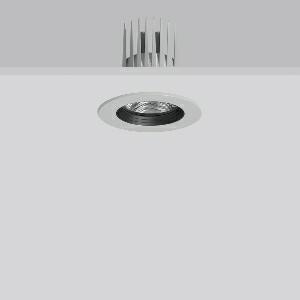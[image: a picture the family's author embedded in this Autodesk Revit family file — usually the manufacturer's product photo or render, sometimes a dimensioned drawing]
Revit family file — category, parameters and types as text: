
# Revit family: heledon_mini_e_901740_004_2_76_123c
name_source: partatom
category: Lighting Fixtures
units: mm (PartAtom-declared; Revit-internal decimal feet)

## family parameters
Cut with Voids When Loaded = No
Host = Face
Light Source = No
Part Type = Normal
Room Calculation Point = No
Round Connector Dimension = Use Diameter
Shared = No

## types (1)
- HELEDON mini E (1 x LED Modul 927, 2400 lm, 2700)
    Apparent Load = 20 VA
    Approval mark = CE
    CIE Flux Codes = 100 100 100 100 100
    Color Rendering = 92
    Color Temperature = 2700
    Default Elevation = 1800 mm
    Description = Series: HELEDON mini
Round recessed downlight. Housing: die-cast aluminium, powder-coated. Black plastic ring and recessed LED to prevent glare from the side. Optical assembly with reflector made of MIRO-Silver with 98% total light reflection for outstanding efficiency - can be changed without tools. Best colour rendering index Ra>90. Suitable for Recessed ceiling mounting. Installation without tools thanks to spring fastening system. Including separate LED converter with connecting cable 600 mm.High quality converter without flickering and stroboscopic effect. Through-wiring box (5 pole) available as accessory. The following accessories can be mounted without use of tools: interchangeable lenses, decorative glasses, honeycomb louvre, clear and frosted diffusers, white interchangeable plastic ring. 
Colour: silver
Diameter: 124 mm
Height: 3 mm
Cut-out diameter: 114 mm
Recess height: 170 mm
Luminaire: recess height: 120 mm
Lamp: LED
Socket: without socket
Colour temperature: 2700K
Colour rendering index (CRI): 92
System power: 20 W
Rated luminous flux: 2400 lm
Luminous efficiency: 120 lm/W
Control gear: Converter, dimmable, DALI
Protection class: II
Type of protection: IP 20
    Height = 0 mm  [stored 0 ft]
    Lamp = 1 x LED Modul 927
    Lamp Light Flux = 2400 lm
    Lamp count = 1
    Length = 124 mm  [stored 0.406824 ft]
    Lifetime = 50000 h
    Luminous efficacy = 120 lm/W
    Manufacturer = RZB
    ModVariant = No
    Model = 901740.004.2.76
    Mounting Place = Ceiling
    Mounting Type = Recessed
    Number of Poles = 1
    OnlyDefault = Yes
    Power Factor = 1
    Product Name = HELEDON mini E
    Product group = Recessed downlights
    ProductGroupID = 402
    Protection Class = Protection class II
    Protection Degree = IP 20
    RLX_Detail_Level = 1
    RLX_Emergency_Light_Flux = 0 lm
    RLX_Emergency_Type = 0
    RLX_Emergency_Type_DB = No
    RlxData = <blob elided: 124633 chars, md5=232a8786>
    Socket = socket
    Standby Power = 0 W
    System Light Flux = 2400 lm
    System Power = 20 W
    Type Comments = Product without accessories
    Type Image = 901657.004.jpg
    URL = http://relux.com
    VarID = ---
    Voltage = 230 V
    Voltage Range = 220-240 V
    Weight = 0.00 kg
    Width = 0 mm  [stored 0 ft]

note: [stored X ft] marks values corroborated as IEEE doubles in the binary element streams (Revit-internal decimal feet)

## geometry (parser evidence)
native form markers: Blend x4, Sweep x12
no freeform markers — native parametric forms only
